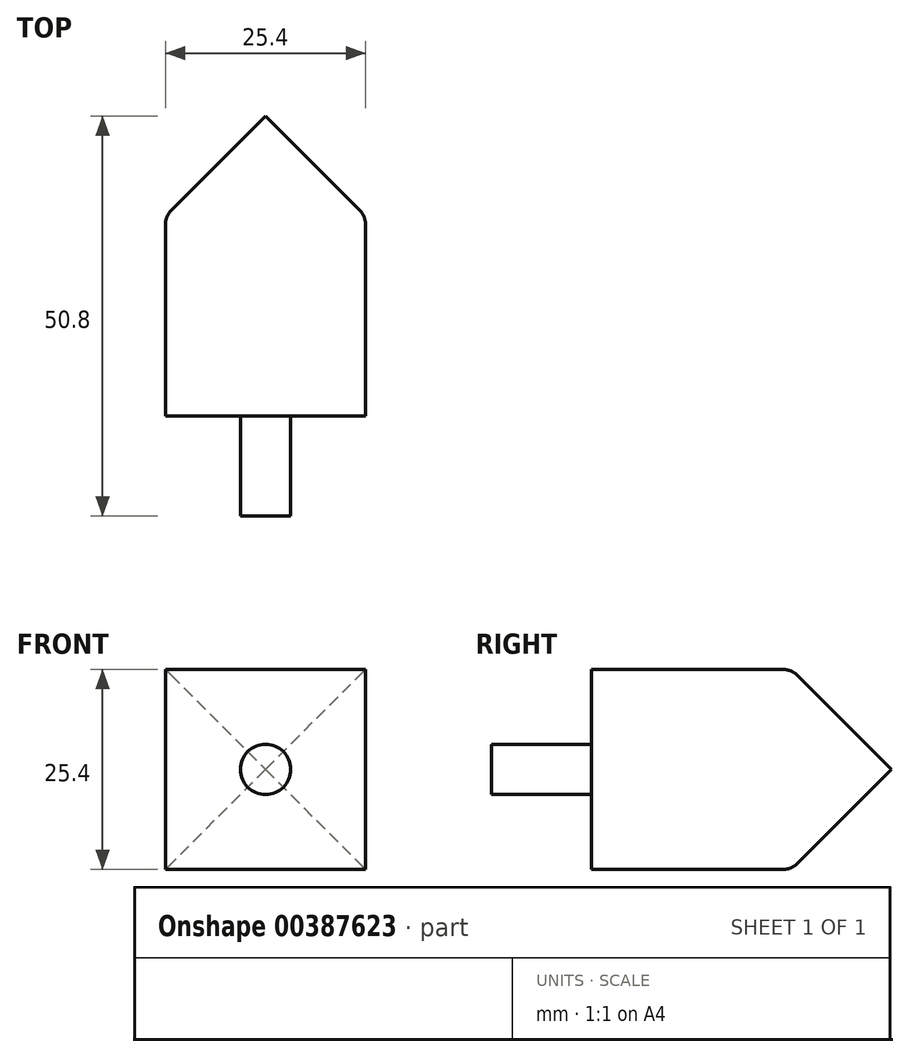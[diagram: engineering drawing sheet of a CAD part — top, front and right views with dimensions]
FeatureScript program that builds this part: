
annotation { "Feature Type Name" : "Feature", "Feature Type Description" : "" }
export const myFeature = defineFeature(function(context is Context, id is Id, definition is map)
    precondition{}
    {
        {
            var Q0;
            Q0=qCreatedBy(makeId("Front.planeOp"),FACE);
            var sketch = newSketch(context, id + "F0", { "sketchPlane" : qUnion([Q0])});
            skLineSegment(sketch, "E0.bottom", {"start": v(-23.58, 16.74) * mm, "end": v(1.82, 16.74) * mm});
            skLineSegment(sketch, "E0.top", {"start": v(-23.58, -8.66) * mm, "end": v(1.82, -8.66) * mm});
            skLineSegment(sketch, "E0.left", {"start": v(-23.58, 16.74) * mm, "end": v(-23.58, -8.66) * mm});
            skLineSegment(sketch, "E0.right", {"start": v(1.82, 16.74) * mm, "end": v(1.82, -8.66) * mm});
            skSolve(sketch);
        }
        {
            var Q0;
            Q0 = qSketchRegion(id + "F0", true);
            extrude(context, id + "F1", {"entities" : qUnion([Q0]), "depth" : 38.1 * mm});
        }
        {
            var Q0;
            Q0=makeQuery(id+"F1.opExtrude","CAP_FACE",FACE,{"disambiguationData":[OSD([sQuery(id+"F0.wireOp",EDGE,"E0.bottom"),sQuery(id+"F0.wireOp",EDGE,"E0.top"),sQuery(id+"F0.wireOp",EDGE,"E0.left"),sQuery(id+"F0.wireOp",EDGE,"E0.right")])],"isStart":false});
            var sketch = newSketch(context, id + "F2", { "sketchPlane" : qUnion([Q0])});
            skCircle(sketch, "E1", {"center": v(-10.88, 4.04) * mm, "radius": 3.2 * mm});
            skPoint(sketch, "E1.centerSnap0", {"position": v(1.82, 4.04) * mm});
            skPoint(sketch, "E1.centerSnap1", {"position": v(-10.88, 16.74) * mm});
            skSolve(sketch);
        }
        {
            var Q0;
            Q0=makeQuery(id+"F2.imprint","IMPRINT",FACE,{"disambiguationData":[TD([[makeQuery(id+"F2.imprint","IMPRINT",EDGE,{"derivedFrom":sQuery(id+"F2.wireOp",EDGE,"E1")}),1.0]])]});
            extrude(context, id + "F3", {"entities" : qUnion([Q0]), "operationType" : NewBodyOperationType.ADD, "depth" : 12.7 * mm});
        }
        {
            var Q0;
            Q0=makeQuery(id+"F1.opExtrude","CAP_EDGE",EDGE,{"disambiguationData":[OSD([sQuery(id+"F0.wireOp",EDGE,"E0.bottom")])],"isStart":true});
            var Q1;
            Q1=makeQuery(id+"F1.opExtrude","CAP_EDGE",EDGE,{"disambiguationData":[OSD([sQuery(id+"F0.wireOp",EDGE,"E0.top")])],"isStart":true});
            var Q2;
            Q2=makeQuery(id+"F1.opExtrude","CAP_EDGE",EDGE,{"disambiguationData":[OSD([sQuery(id+"F0.wireOp",EDGE,"E0.right")])],"isStart":true});
            var Q3;
            Q3=makeQuery(id+"F1.opExtrude","CAP_EDGE",EDGE,{"disambiguationData":[OSD([sQuery(id+"F0.wireOp",EDGE,"E0.left")])],"isStart":true});
            chamfer(context, id + "F4", {"entities" : qUnion([Q0, Q1, Q2, Q3]), "width" : 12.7 * mm, "tangentPropagation" : true});
        }
        {
            var Q0;
            {var subQ0=sQuery(id+"F0.wireOp",EDGE,"E0.left");Q0=makeQuery(id+"F4.opChamfer","BLEND_EDGE",EDGE,{"blendedFrom":[makeQuery(id+"F1.opExtrude","CAP_EDGE",EDGE,{"disambiguationData":[OSD([subQ0])],"isStart":true}),makeQuery(id+"F1.opExtrude","SWEPT_FACE",FACE,{"disambiguationData":[OSD([subQ0])]})],"blendedInto":[makeQuery(id+"F1.opExtrude","SWEPT_FACE",FACE,{"disambiguationData":[OSD([subQ0])]})]});}
            var Q1;
            {var subQ0=sQuery(id+"F0.wireOp",EDGE,"E0.bottom");Q1=makeQuery(id+"F4.opChamfer","BLEND_EDGE",EDGE,{"blendedFrom":[makeQuery(id+"F1.opExtrude","CAP_EDGE",EDGE,{"disambiguationData":[OSD([subQ0])],"isStart":true}),makeQuery(id+"F1.opExtrude","SWEPT_FACE",FACE,{"disambiguationData":[OSD([subQ0])]})],"blendedInto":[makeQuery(id+"F1.opExtrude","SWEPT_FACE",FACE,{"disambiguationData":[OSD([subQ0])]})]});}
            var Q2;
            {var subQ0=sQuery(id+"F0.wireOp",EDGE,"E0.right");Q2=makeQuery(id+"F4.opChamfer","BLEND_EDGE",EDGE,{"blendedFrom":[makeQuery(id+"F1.opExtrude","CAP_EDGE",EDGE,{"disambiguationData":[OSD([subQ0])],"isStart":true}),makeQuery(id+"F1.opExtrude","SWEPT_FACE",FACE,{"disambiguationData":[OSD([subQ0])]})],"blendedInto":[makeQuery(id+"F1.opExtrude","SWEPT_FACE",FACE,{"disambiguationData":[OSD([subQ0])]})]});}
            var Q3;
            {var subQ0=sQuery(id+"F0.wireOp",EDGE,"E0.top");Q3=makeQuery(id+"F4.opChamfer","BLEND_EDGE",EDGE,{"blendedFrom":[makeQuery(id+"F1.opExtrude","CAP_EDGE",EDGE,{"disambiguationData":[OSD([subQ0])],"isStart":true}),makeQuery(id+"F1.opExtrude","SWEPT_FACE",FACE,{"disambiguationData":[OSD([subQ0])]})],"blendedInto":[makeQuery(id+"F1.opExtrude","SWEPT_FACE",FACE,{"disambiguationData":[OSD([subQ0])]})]});}
            fillet(context, id + "F5", {"entities" : qUnion([Q0, Q1, Q2, Q3]), "radius" : 2.54 * mm, "tangentPropagation" : true, "allowEdgeOverflow" : false});
        }
    });
